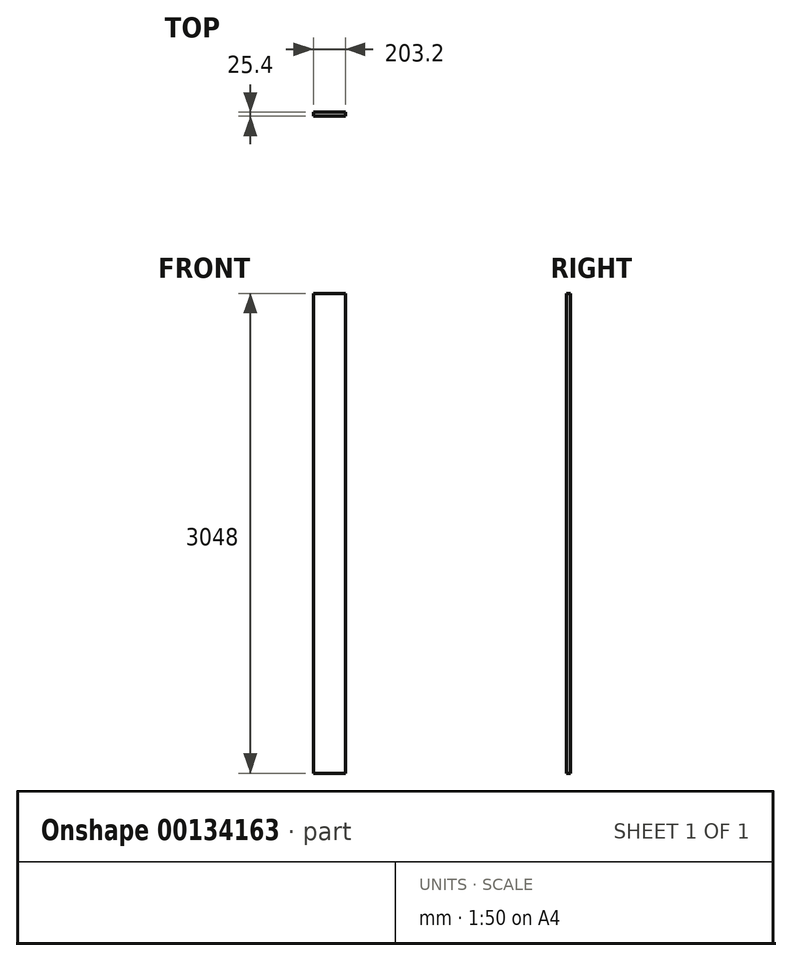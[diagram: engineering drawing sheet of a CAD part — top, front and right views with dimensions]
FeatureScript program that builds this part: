
annotation { "Feature Type Name" : "Feature", "Feature Type Description" : "" }
export const myFeature = defineFeature(function(context is Context, id is Id, definition is map)
    precondition{}
    {
        {
            var Q0;
            Q0=qCreatedBy(makeId("Top.planeOp"),FACE);
            var sketch = newSketch(context, id + "F0", { "sketchPlane" : qUnion([Q0])});
            skLineSegment(sketch, "E0.bottom", {"start": v(0, 0) * mm, "end": v(203.2, 0) * mm});
            skLineSegment(sketch, "E0.top", {"start": v(0, -25.4) * mm, "end": v(203.2, -25.4) * mm});
            skLineSegment(sketch, "E0.left", {"start": v(0, 0) * mm, "end": v(0, -25.4) * mm});
            skLineSegment(sketch, "E0.right", {"start": v(203.2, 0) * mm, "end": v(203.2, -25.4) * mm});
            skSolve(sketch);
        }
        {
            var Q0;
            Q0 = qSketchRegion(id + "F0", true);
            extrude(context, id + "F1", {"entities" : qUnion([Q0]), "depth" : 3048 * mm});
        }
    });
